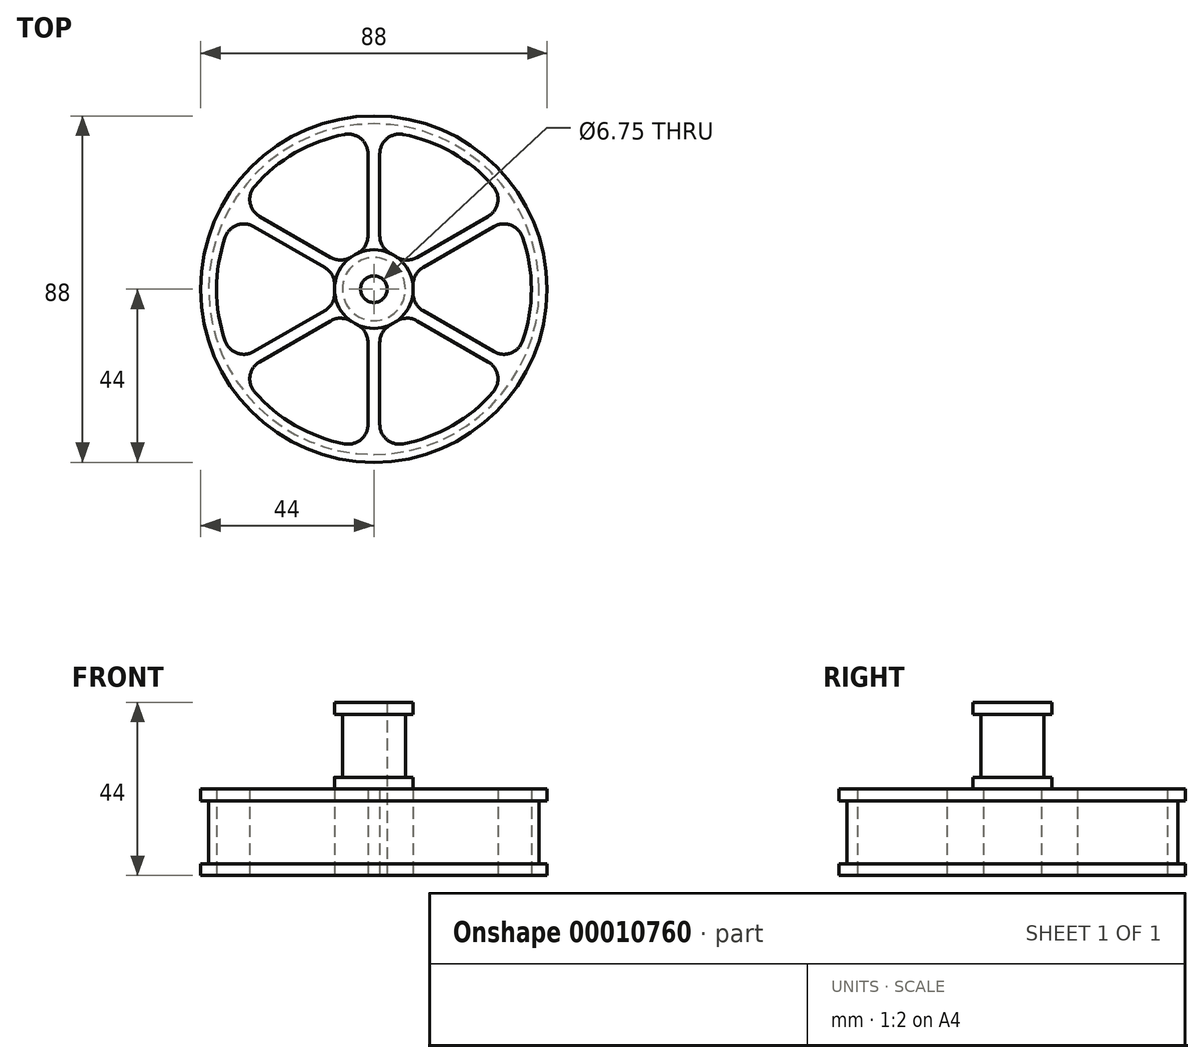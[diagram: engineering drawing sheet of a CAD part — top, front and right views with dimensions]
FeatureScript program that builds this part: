
annotation { "Feature Type Name" : "Feature", "Feature Type Description" : "" }
export const myFeature = defineFeature(function(context is Context, id is Id, definition is map)
    precondition{}
    {
        {
            var Q0;
            Q0=qCreatedBy(makeId("Top.planeOp"),FACE);
            var sketch = newSketch(context, id + "F0", { "sketchPlane" : qUnion([Q0])});
            skCircle(sketch, "E0", {"center": v(0, 0) * mm, "radius": 8 * mm});
            skCircle(sketch, "E1.0", {"center": v(0, 0) * mm, "radius": 10 * mm});
            skCircle(sketch, "E2", {"center": v(0, 0) * mm, "radius": 3.38 * mm});
            skCircle(sketch, "E3", {"center": v(0, 0) * mm, "radius": 42 * mm});
            skCircle(sketch, "E4.0", {"center": v(0, 0) * mm, "radius": 44 * mm});
            skLineSegment(sketch, "E5", {"start": v(-1.5, -9.89) * mm, "end": v(-1.5, -39.97) * mm});
            skLineSegment(sketch, "E6", {"start": v(1.5, -9.89) * mm, "end": v(1.5, -39.97) * mm});
            skLineSegment(sketch, "E7", {"start": v(-1.5, -24.93) * mm, "end": v(1.5, -24.93) * mm, "construction": true});
            skPoint(sketch, "E8", {"position": v(0, -24.93) * mm});
            skLineSegment(sketch, "E9", {"start": v(0, -24.93) * mm, "end": v(0, 0) * mm, "construction": true});
            skCircle(sketch, "E10.0", {"center": v(0, 0) * mm, "radius": 40 * mm});
            skLineSegment(sketch, "E11.1.0", {"start": v(9.31, -3.64) * mm, "end": v(35.37, -18.69) * mm});
            skLineSegment(sketch, "E11.1.1", {"start": v(7.81, -6.24) * mm, "end": v(33.87, -21.28) * mm});
            skLineSegment(sketch, "E11.2.0", {"start": v(7.81, 6.24) * mm, "end": v(33.87, 21.28) * mm});
            skLineSegment(sketch, "E11.2.1", {"start": v(9.31, 3.64) * mm, "end": v(35.37, 18.69) * mm});
            skLineSegment(sketch, "E11.3.0", {"start": v(-1.5, 9.89) * mm, "end": v(-1.5, 39.97) * mm});
            skLineSegment(sketch, "E11.3.1", {"start": v(1.5, 9.89) * mm, "end": v(1.5, 39.97) * mm});
            skLineSegment(sketch, "E11.4.0", {"start": v(-9.31, 3.64) * mm, "end": v(-35.37, 18.69) * mm});
            skLineSegment(sketch, "E11.4.1", {"start": v(-7.81, 6.24) * mm, "end": v(-33.87, 21.28) * mm});
            skLineSegment(sketch, "E11.5.0", {"start": v(-7.81, -6.24) * mm, "end": v(-33.87, -21.28) * mm});
            skLineSegment(sketch, "E11.5.1", {"start": v(-9.31, -3.64) * mm, "end": v(-35.37, -18.69) * mm});
            skSolve(sketch);
        }
        {
            var Q0;
            Q0=makeQuery(id+"F0.imprint","IMPRINT",FACE,{"disambiguationData":[TD([[makeQuery(id+"F0.imprint","IMPRINT",EDGE,{"derivedFrom":sQuery(id+"F0.wireOp",EDGE,"E0")}),1.0]])]});
            extrude(context, id + "F1", {"entities" : qUnion([Q0]), "depth" : 22 * mm});
        }
        {
            var Q0;
            Q0=makeQuery(id+"F0.imprint","IMPRINT",FACE,{"disambiguationData":[TD([[makeQuery(id+"F0.imprint","IMPRINT",EDGE,{"derivedFrom":sQuery(id+"F0.wireOp",EDGE,"E0")}),-1.0]])]});
            extrude(context, id + "F2", {"entities" : qUnion([Q0]), "operationType" : NewBodyOperationType.ADD, "depth" : 22 * mm, "hasSecondDirection" : true, "secondDirectionOppositeDirection" : false, "secondDirectionDepth" : 19 * mm});
        }
        {
            var Q0;
            Q0=makeQuery(id+"F0.imprint","IMPRINT",FACE,{"disambiguationData":[TD([[makeQuery(id+"F0.imprint","IMPRINT",EDGE,{"derivedFrom":sQuery(id+"F0.wireOp",EDGE,"E0")}),-1.0]])]});
            extrude(context, id + "F3", {"entities" : qUnion([Q0]), "operationType" : NewBodyOperationType.ADD, "depth" : 3 * mm});
        }
        {
            var Q0;
            Q0=makeQuery(id+"F1.opExtrude","SWEPT_BODY",BODY,{"disambiguationData":[OSD([sQuery(id+"F0.wireOp",EDGE,"E0"),sQuery(id+"F0.wireOp",EDGE,"E2")])]});
            transform(context, id + "F4", {"entities" : qUnion([Q0]), "transformType" : TransformType.TRANSLATION_3D, "dx" : 0 * mm, "dy" : 0 * mm, "dz" : 22 * mm, "makeCopy" : false});
        }
        {
            var Q0;
            Q0=makeQuery(id+"F0.imprint","IMPRINT",FACE,{"disambiguationData":[TD([[makeQuery(id+"F0.imprint","IMPRINT",EDGE,{"derivedFrom":sQuery(id+"F0.wireOp",EDGE,"E0")}),1.0]])]});
            var Q1;
            Q1=makeQuery(id+"F0.imprint","IMPRINT",FACE,{"disambiguationData":[TD([[makeQuery(id+"F0.imprint","IMPRINT",EDGE,{"derivedFrom":sQuery(id+"F0.wireOp",EDGE,"E0")}),-1.0]])]});
            var Q2;
            {var subQ1=sQuery(id+"F0.wireOp",EDGE,"E11.3.0");Q2=makeQuery(id+"F0.imprint","IMPRINT",FACE,{"disambiguationData":[TD([[makeQuery(id+"F0.imprint","IMPRINT",EDGE,{"derivedFrom":subQ1}),-1.0]])]});}
            var Q3;
            {var subQ1=sQuery(id+"F0.wireOp",EDGE,"E11.2.0");Q3=makeQuery(id+"F0.imprint","IMPRINT",FACE,{"disambiguationData":[TD([[makeQuery(id+"F0.imprint","IMPRINT",EDGE,{"derivedFrom":subQ1}),-1.0]])]});}
            var Q4;
            {var subQ1=sQuery(id+"F0.wireOp",EDGE,"E11.4.0");Q4=makeQuery(id+"F0.imprint","IMPRINT",FACE,{"disambiguationData":[TD([[makeQuery(id+"F0.imprint","IMPRINT",EDGE,{"derivedFrom":subQ1}),-1.0]])]});}
            var Q5;
            {var subQ1=sQuery(id+"F0.wireOp",EDGE,"E11.5.0");Q5=makeQuery(id+"F0.imprint","IMPRINT",FACE,{"disambiguationData":[TD([[makeQuery(id+"F0.imprint","IMPRINT",EDGE,{"derivedFrom":subQ1}),-1.0]])]});}
            var Q6;
            {var subQ1=sQuery(id+"F0.wireOp",EDGE,"E11.1.0");Q6=makeQuery(id+"F0.imprint","IMPRINT",FACE,{"disambiguationData":[TD([[makeQuery(id+"F0.imprint","IMPRINT",EDGE,{"derivedFrom":subQ1}),-1.0]])]});}
            var Q7;
            {var subQ2=sQuery(id+"F0.wireOp",EDGE,"E5");Q7=makeQuery(id+"F0.imprint","IMPRINT",FACE,{"disambiguationData":[TD([[makeQuery(id+"F0.imprint","IMPRINT",EDGE,{"derivedFrom":subQ2}),1.0]])]});}
            var Q8;
            Q8=makeQuery(id+"F0.imprint","IMPRINT",FACE,{"disambiguationData":[TD([[makeQuery(id+"F0.imprint","IMPRINT",EDGE,{"derivedFrom":sQuery(id+"F0.wireOp",EDGE,"E3")}),1.0]])]});
            extrude(context, id + "F5", {"entities" : qUnion([Q0, Q1, Q2, Q3, Q4, Q5, Q6, Q7, Q8]), "operationType" : NewBodyOperationType.ADD, "depth" : 22 * mm});
        }
        {
            var Q0;
            Q0=makeQuery(id+"F0.imprint","IMPRINT",FACE,{"disambiguationData":[TD([[makeQuery(id+"F0.imprint","IMPRINT",EDGE,{"derivedFrom":sQuery(id+"F0.wireOp",EDGE,"E3")}),-1.0]])]});
            extrude(context, id + "F6", {"entities" : qUnion([Q0]), "operationType" : NewBodyOperationType.ADD, "depth" : 22 * mm, "hasSecondDirection" : true, "secondDirectionOppositeDirection" : false, "secondDirectionDepth" : 19 * mm});
        }
        {
            var Q0;
            Q0=makeQuery(id+"F0.imprint","IMPRINT",FACE,{"disambiguationData":[TD([[makeQuery(id+"F0.imprint","IMPRINT",EDGE,{"derivedFrom":sQuery(id+"F0.wireOp",EDGE,"E3")}),-1.0]])]});
            extrude(context, id + "F7", {"entities" : qUnion([Q0]), "operationType" : NewBodyOperationType.ADD, "depth" : 3 * mm});
        }
        {
            var Q0;
            Q0=makeQuery(id+"F3.opExtrude","CAP_EDGE",EDGE,{"disambiguationData":[OSD([sQuery(id+"F0.wireOp",EDGE,"E0")])],"isStart":false});
            var Q1;
            Q1=makeQuery(id+"F2.opExtrude","CAP_EDGE",EDGE,{"disambiguationData":[OSD([sQuery(id+"F0.wireOp",EDGE,"E0")])],"isStart":true});
            var Q2;
            Q2=makeQuery(id+"F7.opExtrude","CAP_EDGE",EDGE,{"disambiguationData":[OSD([sQuery(id+"F0.wireOp",EDGE,"E3")])],"isStart":false});
            var Q3;
            Q3=makeQuery(id+"F6.opExtrude","CAP_EDGE",EDGE,{"disambiguationData":[OSD([sQuery(id+"F0.wireOp",EDGE,"E3")])],"isStart":true});
            var Q4;
            Q4=makeQuery(id+"F5.opExtrude","SWEPT_EDGE",EDGE,{"disambiguationData":[OSD([sQuery(id+"F0.wireOp",EDGE,"E1.0"),sQuery(id+"F0.wireOp",EDGE,"E11.1.0")])]});
            var Q5;
            Q5=makeQuery(id+"F5.opExtrude","SWEPT_EDGE",EDGE,{"disambiguationData":[OSD([sQuery(id+"F0.wireOp",EDGE,"E1.0"),sQuery(id+"F0.wireOp",EDGE,"E11.2.1")])]});
            var Q6;
            Q6=makeQuery(id+"F5.opExtrude","SWEPT_EDGE",EDGE,{"disambiguationData":[OSD([sQuery(id+"F0.wireOp",EDGE,"E1.0"),sQuery(id+"F0.wireOp",EDGE,"E11.1.1")])]});
            var Q7;
            Q7=makeQuery(id+"F5.opExtrude","SWEPT_EDGE",EDGE,{"disambiguationData":[OSD([sQuery(id+"F0.wireOp",EDGE,"E1.0"),sQuery(id+"F0.wireOp",EDGE,"E6")])]});
            var Q8;
            Q8=makeQuery(id+"F5.opExtrude","SWEPT_EDGE",EDGE,{"disambiguationData":[OSD([sQuery(id+"F0.wireOp",EDGE,"E1.0"),sQuery(id+"F0.wireOp",EDGE,"E5")])]});
            var Q9;
            Q9=makeQuery(id+"F5.opExtrude","SWEPT_EDGE",EDGE,{"disambiguationData":[OSD([sQuery(id+"F0.wireOp",EDGE,"E1.0"),sQuery(id+"F0.wireOp",EDGE,"E11.5.0")])]});
            var Q10;
            Q10=makeQuery(id+"F5.opExtrude","SWEPT_EDGE",EDGE,{"disambiguationData":[OSD([sQuery(id+"F0.wireOp",EDGE,"E1.0"),sQuery(id+"F0.wireOp",EDGE,"E11.5.1")])]});
            var Q11;
            Q11=makeQuery(id+"F5.opExtrude","SWEPT_EDGE",EDGE,{"disambiguationData":[OSD([sQuery(id+"F0.wireOp",EDGE,"E1.0"),sQuery(id+"F0.wireOp",EDGE,"E11.4.0")])]});
            var Q12;
            Q12=makeQuery(id+"F5.opExtrude","SWEPT_EDGE",EDGE,{"disambiguationData":[OSD([sQuery(id+"F0.wireOp",EDGE,"E1.0"),sQuery(id+"F0.wireOp",EDGE,"E11.4.1")])]});
            var Q13;
            Q13=makeQuery(id+"F5.opExtrude","SWEPT_EDGE",EDGE,{"disambiguationData":[OSD([sQuery(id+"F0.wireOp",EDGE,"E1.0"),sQuery(id+"F0.wireOp",EDGE,"E11.3.0")])]});
            var Q14;
            Q14=makeQuery(id+"F5.opExtrude","SWEPT_EDGE",EDGE,{"disambiguationData":[OSD([sQuery(id+"F0.wireOp",EDGE,"E1.0"),sQuery(id+"F0.wireOp",EDGE,"E11.3.1")])]});
            var Q15;
            Q15=makeQuery(id+"F5.opExtrude","SWEPT_EDGE",EDGE,{"disambiguationData":[OSD([sQuery(id+"F0.wireOp",EDGE,"E1.0"),sQuery(id+"F0.wireOp",EDGE,"E11.2.0")])]});
            var Q16;
            Q16=makeQuery(id+"F5.opExtrude","SWEPT_EDGE",EDGE,{"disambiguationData":[OSD([sQuery(id+"F0.wireOp",EDGE,"E10.0"),sQuery(id+"F0.wireOp",EDGE,"E11.2.0")])]});
            var Q17;
            Q17=makeQuery(id+"F5.opExtrude","SWEPT_EDGE",EDGE,{"disambiguationData":[OSD([sQuery(id+"F0.wireOp",EDGE,"E10.0"),sQuery(id+"F0.wireOp",EDGE,"E11.1.1")])]});
            var Q18;
            Q18=makeQuery(id+"F5.opExtrude","SWEPT_EDGE",EDGE,{"disambiguationData":[OSD([sQuery(id+"F0.wireOp",EDGE,"E10.0"),sQuery(id+"F0.wireOp",EDGE,"E11.2.1")])]});
            var Q19;
            Q19=makeQuery(id+"F5.opExtrude","SWEPT_EDGE",EDGE,{"disambiguationData":[OSD([sQuery(id+"F0.wireOp",EDGE,"E10.0"),sQuery(id+"F0.wireOp",EDGE,"E11.3.1")])]});
            var Q20;
            Q20=makeQuery(id+"F5.opExtrude","SWEPT_EDGE",EDGE,{"disambiguationData":[OSD([sQuery(id+"F0.wireOp",EDGE,"E10.0"),sQuery(id+"F0.wireOp",EDGE,"E11.1.0")])]});
            var Q21;
            Q21=makeQuery(id+"F5.opExtrude","SWEPT_EDGE",EDGE,{"disambiguationData":[OSD([sQuery(id+"F0.wireOp",EDGE,"E6"),sQuery(id+"F0.wireOp",EDGE,"E10.0")])]});
            var Q22;
            Q22=makeQuery(id+"F5.opExtrude","SWEPT_EDGE",EDGE,{"disambiguationData":[OSD([sQuery(id+"F0.wireOp",EDGE,"E5"),sQuery(id+"F0.wireOp",EDGE,"E10.0")])]});
            var Q23;
            Q23=makeQuery(id+"F5.opExtrude","SWEPT_EDGE",EDGE,{"disambiguationData":[OSD([sQuery(id+"F0.wireOp",EDGE,"E10.0"),sQuery(id+"F0.wireOp",EDGE,"E11.5.0")])]});
            var Q24;
            Q24=makeQuery(id+"F5.opExtrude","SWEPT_EDGE",EDGE,{"disambiguationData":[OSD([sQuery(id+"F0.wireOp",EDGE,"E10.0"),sQuery(id+"F0.wireOp",EDGE,"E11.5.1")])]});
            var Q25;
            Q25=makeQuery(id+"F5.opExtrude","SWEPT_EDGE",EDGE,{"disambiguationData":[OSD([sQuery(id+"F0.wireOp",EDGE,"E10.0"),sQuery(id+"F0.wireOp",EDGE,"E11.4.0")])]});
            var Q26;
            Q26=makeQuery(id+"F5.opExtrude","SWEPT_EDGE",EDGE,{"disambiguationData":[OSD([sQuery(id+"F0.wireOp",EDGE,"E10.0"),sQuery(id+"F0.wireOp",EDGE,"E11.4.1")])]});
            var Q27;
            Q27=makeQuery(id+"F5.opExtrude","SWEPT_EDGE",EDGE,{"disambiguationData":[OSD([sQuery(id+"F0.wireOp",EDGE,"E10.0"),sQuery(id+"F0.wireOp",EDGE,"E11.3.0")])]});
            var Q28;
            {var subQ0=sQuery(id+"F0.wireOp",EDGE,"E1.0");var subQ5=sQuery(id+"F0.wireOp",EDGE,"E5");Q28=makeQuery(id+"F5.boolean.opBoolean","SPLIT",EDGE,{"disambiguationData":[TD([makeQuery(id+"F5.opExtrude","SWEPT_FACE",FACE,{"disambiguationData":[OSD([subQ5])]})])],"derivedFrom":makeQuery(id+"F3.opExtrude","CAP_EDGE",EDGE,{"disambiguationData":[OSD([subQ0])],"isStart":true})});}
            var Q29;
            {var subQ0=sQuery(id+"F0.wireOp",EDGE,"E1.0");var subQ1=sQuery(id+"F0.wireOp",EDGE,"E11.1.0");Q29=makeQuery(id+"F5.boolean.opBoolean","SPLIT",EDGE,{"disambiguationData":[TD([makeQuery(id+"F5.opExtrude","SWEPT_FACE",FACE,{"disambiguationData":[OSD([subQ1])]})])],"derivedFrom":makeQuery(id+"F3.opExtrude","CAP_EDGE",EDGE,{"disambiguationData":[OSD([subQ0])],"isStart":true})});}
            var Q30;
            {var subQ0=sQuery(id+"F0.wireOp",EDGE,"E1.0");var subQ2=sQuery(id+"F0.wireOp",EDGE,"E11.5.0");Q30=makeQuery(id+"F5.boolean.opBoolean","SPLIT",EDGE,{"disambiguationData":[TD([makeQuery(id+"F5.opExtrude","SWEPT_FACE",FACE,{"disambiguationData":[OSD([subQ2])]})])],"derivedFrom":makeQuery(id+"F3.opExtrude","CAP_EDGE",EDGE,{"disambiguationData":[OSD([subQ0])],"isStart":true})});}
            var Q31;
            {var subQ0=sQuery(id+"F0.wireOp",EDGE,"E1.0");var subQ1=sQuery(id+"F0.wireOp",EDGE,"E11.2.0");Q31=makeQuery(id+"F5.boolean.opBoolean","SPLIT",EDGE,{"disambiguationData":[TD([makeQuery(id+"F5.opExtrude","SWEPT_FACE",FACE,{"disambiguationData":[OSD([subQ1])]})])],"derivedFrom":makeQuery(id+"F3.opExtrude","CAP_EDGE",EDGE,{"disambiguationData":[OSD([subQ0])],"isStart":true})});}
            var Q32;
            {var subQ0=sQuery(id+"F0.wireOp",EDGE,"E1.0");var subQ2=sQuery(id+"F0.wireOp",EDGE,"E11.3.0");Q32=makeQuery(id+"F5.boolean.opBoolean","SPLIT",EDGE,{"disambiguationData":[TD([makeQuery(id+"F5.opExtrude","SWEPT_FACE",FACE,{"disambiguationData":[OSD([subQ2])]})])],"derivedFrom":makeQuery(id+"F3.opExtrude","CAP_EDGE",EDGE,{"disambiguationData":[OSD([subQ0])],"isStart":true})});}
            var Q33;
            {var subQ0=sQuery(id+"F0.wireOp",EDGE,"E1.0");var subQ1=sQuery(id+"F0.wireOp",EDGE,"E11.4.0");Q33=makeQuery(id+"F5.boolean.opBoolean","SPLIT",EDGE,{"disambiguationData":[TD([makeQuery(id+"F5.opExtrude","SWEPT_FACE",FACE,{"disambiguationData":[OSD([subQ1])]})])],"derivedFrom":makeQuery(id+"F3.opExtrude","CAP_EDGE",EDGE,{"disambiguationData":[OSD([subQ0])],"isStart":true})});}
            fillet(context, id + "F8", {"entities" : qUnion([Q0, Q1, Q2, Q3, Q4, Q5, Q6, Q7, Q8, Q9, Q10, Q11, Q12, Q13, Q14, Q15, Q16, Q17, Q18, Q19, Q20, Q21, Q22, Q23, Q24, Q25, Q26, Q27, Q28, Q29, Q30, Q31, Q32, Q33]), "radius" : 5 * mm, "tangentPropagation" : true, "allowEdgeOverflow" : false});
        }
    });
